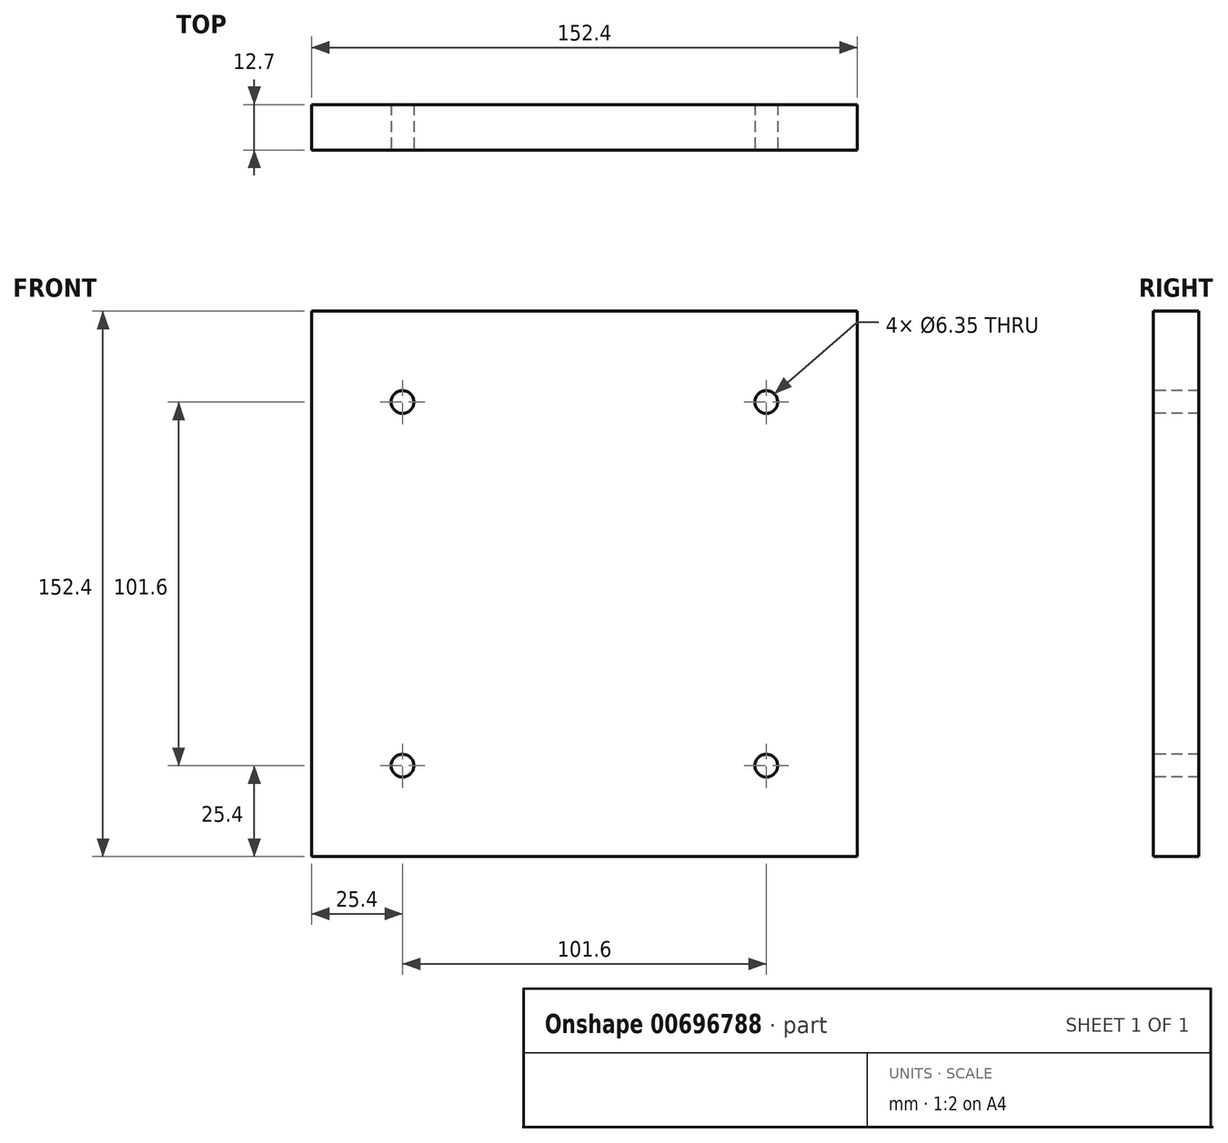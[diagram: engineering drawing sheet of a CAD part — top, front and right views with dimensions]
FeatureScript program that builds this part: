
annotation { "Feature Type Name" : "Feature", "Feature Type Description" : "" }
export const myFeature = defineFeature(function(context is Context, id is Id, definition is map)
    precondition{}
    {
        {
            var Q0;
            Q0=qCreatedBy(makeId("Front.planeOp"),FACE);
            var sketch = newSketch(context, id + "F0", { "sketchPlane" : qUnion([Q0])});
            skLineSegment(sketch, "E0.bottom", {"start": v(76.2, 76.2) * mm, "end": v(-76.2, 76.2) * mm});
            skLineSegment(sketch, "E0.top", {"start": v(76.2, -76.2) * mm, "end": v(-76.2, -76.2) * mm});
            skLineSegment(sketch, "E0.left", {"start": v(76.2, 76.2) * mm, "end": v(76.2, -76.2) * mm});
            skLineSegment(sketch, "E0.right", {"start": v(-76.2, 76.2) * mm, "end": v(-76.2, -76.2) * mm});
            skPoint(sketch, "E0.middle", {"position": v(0, 0) * mm});
            skSolve(sketch);
        }
        {
            var Q0;
            Q0 = qSketchRegion(id + "F0", true);
            extrude(context, id + "F1", {"entities" : qUnion([Q0]), "depth" : 12.7 * mm, "offsetDistance" : 25.4 * mm, "symmetric" : true});
        }
        {
            var Q0;
            Q0=makeQuery(id+"F1.opExtrude","CAP_FACE",FACE,{"disambiguationData":[OSD([sQuery(id+"F0.wireOp",EDGE,"E0.bottom"),sQuery(id+"F0.wireOp",EDGE,"E0.top"),sQuery(id+"F0.wireOp",EDGE,"E0.left"),sQuery(id+"F0.wireOp",EDGE,"E0.right")])],"isStart":false});
            var sketch = newSketch(context, id + "F2", { "sketchPlane" : qUnion([Q0])});
            skLineSegment(sketch, "E1.bottom", {"start": v(50.8, 50.8) * mm, "end": v(-50.8, 50.8) * mm});
            skLineSegment(sketch, "E1.top", {"start": v(50.8, -50.8) * mm, "end": v(-50.8, -50.8) * mm});
            skLineSegment(sketch, "E1.left", {"start": v(50.8, 50.8) * mm, "end": v(50.8, -50.8) * mm});
            skLineSegment(sketch, "E1.right", {"start": v(-50.8, 50.8) * mm, "end": v(-50.8, -50.8) * mm});
            skPoint(sketch, "E1.middle", {"position": v(0, 0) * mm});
            skSolve(sketch);
        }
        {
            var Q0;
            Q0=sQuery(id+"F2.wireOp",VERTEX,"E1.right.start");
            var Q1;
            Q1=sQuery(id+"F2.wireOp",VERTEX,"E1.left.start");
            var Q2;
            Q2=sQuery(id+"F2.wireOp",VERTEX,"E1.left.end");
            var Q3;
            Q3=sQuery(id+"F2.wireOp",VERTEX,"E1.top.end");
            var Q4;
            Q4=makeQuery(id+"F1.opExtrude","SWEPT_BODY",BODY,{"disambiguationData":[OSD([sQuery(id+"F0.wireOp",EDGE,"E0.bottom"),sQuery(id+"F0.wireOp",EDGE,"E0.top"),sQuery(id+"F0.wireOp",EDGE,"E0.left"),sQuery(id+"F0.wireOp",EDGE,"E0.right")])]});
            hole(context, id + "F3", {"style" : HoleStyle.SIMPLE, "endStyle" : HoleEndStyle.THROUGH, "holeDiameter" : 6.35 * mm, "majorDiameter" : 6.35 * mm, "isTappedThrough" : true, "tappedDepth" : 12.7 * mm, "tapClearance" : 3, "startFromSketch" : true, "locations" : qUnion([Q0, Q1, Q2, Q3]), "scope" : qUnion([Q4])});
        }
    });
